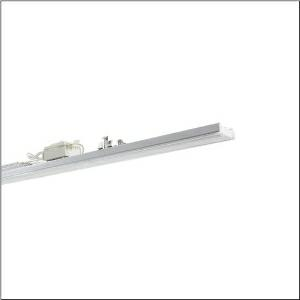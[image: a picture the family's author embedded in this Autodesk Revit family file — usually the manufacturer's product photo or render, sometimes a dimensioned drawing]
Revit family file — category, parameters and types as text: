
# Revit family: licross_21_recessed_mo_52tl18dn495g
name_source: partatom
category: Lighting Fixtures
units: mm (PartAtom-declared; Revit-internal decimal feet)

## family parameters
Cut with Voids When Loaded = No
Host = Face
Light Source = No
Part Type = Normal
Room Calculation Point = No
Round Connector Dimension = Use Diameter
Shared = No

## types (1)
- --- (1 x LED, 9990 lm, 58 W, 4000K)
    Apparent Load = 58 VA
    CIE Flux Codes = 79 95 99 100 100
    Color Rendering = 80
    Color Temperature = 4000K
    Default Elevation = 1800 mm
    Description = Licross 21 Recessed MO, luminaire insert, of sheet steel, galvanised, coil coated, white, length: 1.500mm, width: 66mm, height: 67mm, LED rated luminous flux: 9.990lm, light colour: 840, SDCM (Standard Deviation of Colour Matching)MacAdam ≤ 3 SDCM (initial), control gear: DALI 2, with plug, 5-pole, with phase selection, mains connection: 220..240V, AC, 50/60Hz, rated input power: 58W, internal wiring halogen-free, primary light control with lens, of plastic, primary optical cover: cover, of PMMA, light emission: direct distribution, primary light characteristic: symmetric, protection rating (complete): IP40, insulation class (complete): insulation class I (protective earthing), certification: CE, ENEC, VDE, UKCA, protection symbol: D if used in an environment without relevant dust loads with corresponding accessories, impact resistance: IK06, permissible ambient temperature for indoor applications: -25..+35°C, corresponds to IFS (International Featured Standards) requirements for safety and quality in the food industry, reducing of maximum allowable ambient temperature of 5°C with ceiling mounting, LABS conformity tested according to VDMA 24364:2018-05, The light source and the operating device comply with the requirements of the Ecodesign Regulation (EU) 2019/2020 and are replaceable in accordance with this regulation, packaging unit: 1 piece
    Height = 58 mm
    Lamp = 1 x LED
    Lamp Light Flux = 9990 lm
    Lamp Power = 58 W
    Lamp count = 1
    Length = 1500 mm
    Luminous efficacy = 172 lm/W
    Manufacturer = Siteco
    ModVariant = No
    Model = 52TL18DN495G
    Mounting Place = Ceiling
    Mounting Type = Pendant
    Number of Poles = 1
    OnlyDefault = Yes
    Power Factor = 1
    Product Name = Licross 21 Recessed MO
    Product group = luminaire insert | ceiling pendant
    ProductGroupID = 901
    Protection Class = Protection class I
    Protection Degree = IP 40
    RLX_Detail_Level = 1
    RLX_Emergency_Light_Flux = 0 lm
    RLX_Emergency_Type = 0
    RLX_Emergency_Type_DB = No
    RlxData = <blob elided: 24761 chars, md5=7af69470>
    Socket = socket
    Standby Power = 0 W
    System Light Flux = 9990 lm
    System Power = 58 W
    Type Comments = factory setting: luminous flux: 100 % | dim-lin: 254 | 390 mA
    Type Image = l_1296930.jpg
    URL = http://relux.com
    VarID = @adj_126133
    Voltage = 0 V
    Weight = 0.00 kg
    Width = 66 mm

## geometry (parser evidence)
native form markers: Blend x4, Sweep x12
no freeform markers — native parametric forms only
